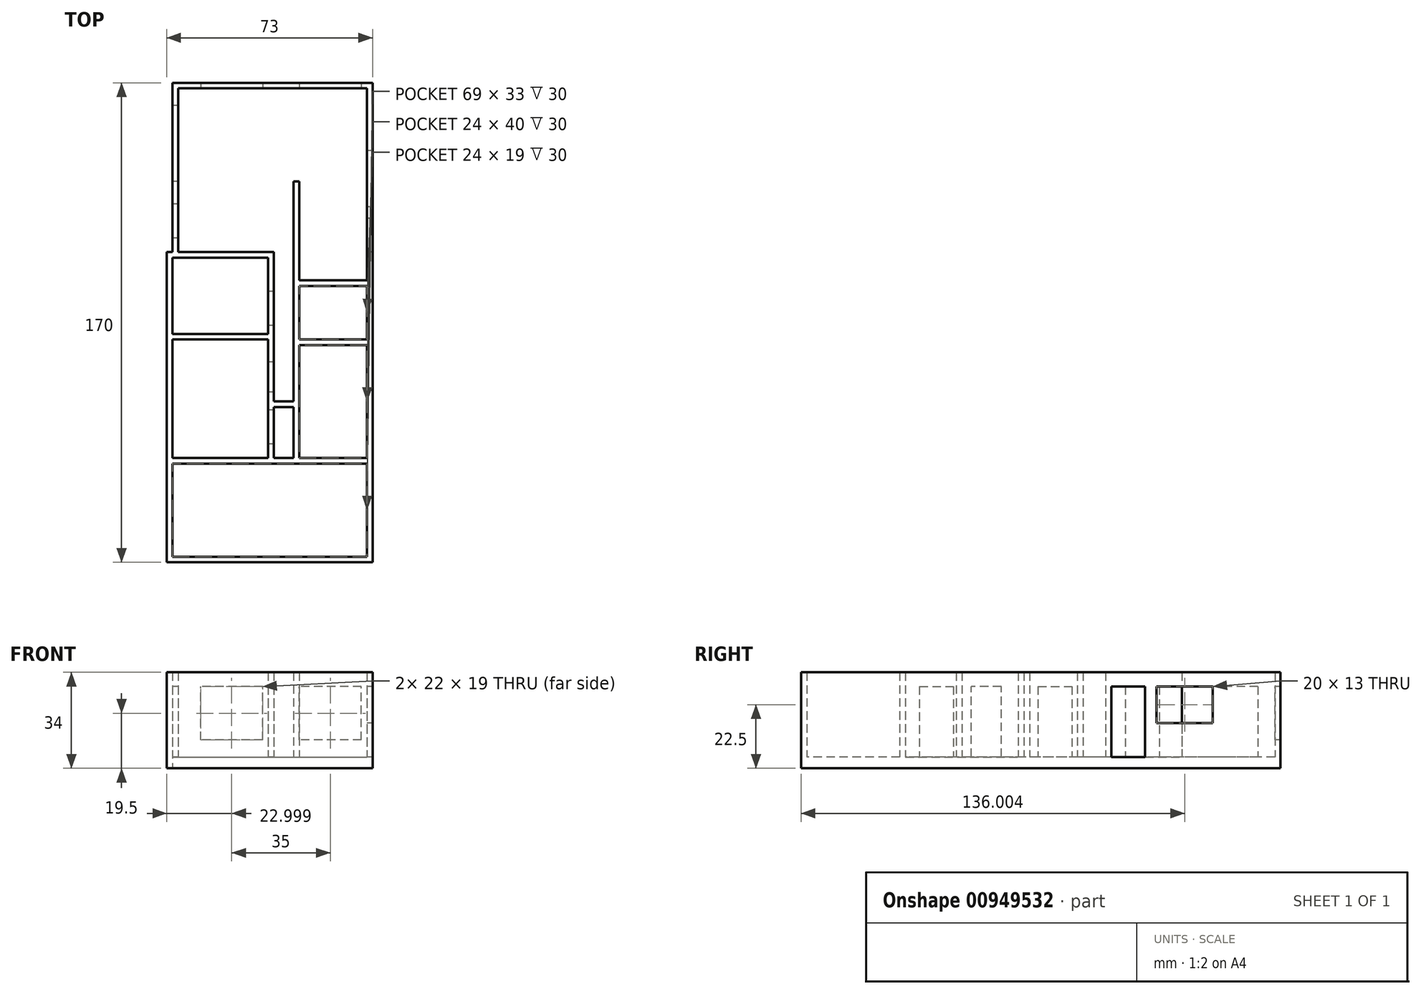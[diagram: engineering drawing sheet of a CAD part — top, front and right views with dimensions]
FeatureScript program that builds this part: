
annotation { "Feature Type Name" : "Feature", "Feature Type Description" : "" }
export const myFeature = defineFeature(function(context is Context, id is Id, definition is map)
    precondition{}
    {
        {
            assignVariable(context, id + "F0", {"name" : "WallWidth", "anyValue" : 2});
        }
        {
            assignVariable(context, id + "F1", {"name" : "Floor", "anyValue" : 4});
        }
        {
            var Q0;
            Q0=qCreatedBy(makeId("Top.planeOp"),FACE);
            var sketch = newSketch(context, id + "F2", { "sketchPlane" : qUnion([Q0])});
            skLineSegment(sketch, "E0.bottom", {"start": v(-13.18, 167.27) * mm, "end": v(57.82, 167.27) * mm});
            skLineSegment(sketch, "E0.top", {"start": v(-13.18, -2.73) * mm, "end": v(57.82, -2.73) * mm});
            skLineSegment(sketch, "E0.left", {"start": v(-13.18, 167.27) * mm, "end": v(-13.18, -2.73) * mm});
            skLineSegment(sketch, "E0.right", {"start": v(57.82, 167.27) * mm, "end": v(57.82, -2.73) * mm});
            skLineSegment(sketch, "E1.bottom", {"start": v(-13.18, -2.73) * mm, "end": v(-15.18, -2.73) * mm});
            skLineSegment(sketch, "E1.top", {"start": v(-13.18, 107.27) * mm, "end": v(-15.18, 107.27) * mm});
            skLineSegment(sketch, "E1.left", {"start": v(-13.18, -2.73) * mm, "end": v(-13.18, 107.27) * mm});
            skLineSegment(sketch, "E1.right", {"start": v(-15.18, -2.73) * mm, "end": v(-15.18, 107.27) * mm});
            skSolve(sketch);
        }
        {
            var Q0;
            Q0=qSketchRegion(id+"F2",true);
            extrude(context, id + "F3", {"entities" : qUnion([Q0]), "depth" : (getVariable(context, 'Floor')) * mm, "offsetDistance" : 25 * mm});
        }
        {
            var Q0;
            Q0=makeQuery(id+"F3.opExtrude","CAP_FACE",FACE,{"disambiguationData":[OSD([sQuery(id+"F2.wireOp",EDGE,"E0.bottom"),sQuery(id+"F2.wireOp",EDGE,"E0.top"),sQuery(id+"F2.wireOp",EDGE,"E0.left"),sQuery(id+"F2.wireOp",EDGE,"E0.right"),sQuery(id+"F2.wireOp",EDGE,"E1.bottom"),sQuery(id+"F2.wireOp",EDGE,"E1.top"),sQuery(id+"F2.wireOp",EDGE,"E1.right")])],"isStart":false});
            var sketch = newSketch(context, id + "F4", { "sketchPlane" : qUnion([Q0])});
            skLineSegment(sketch, "E2.bottom", {"start": v(-15.18, -2.73) * mm, "end": v(57.82, -2.73) * mm});
            skLineSegment(sketch, "E2.top", {"start": v(-15.18, -0.73) * mm, "end": v(57.82, -0.73) * mm});
            skLineSegment(sketch, "E2.left", {"start": v(-15.18, -2.73) * mm, "end": v(-15.18, -0.73) * mm});
            skLineSegment(sketch, "E2.right", {"start": v(57.82, -2.73) * mm, "end": v(57.82, -0.73) * mm});
            skLineSegment(sketch, "E3.bottom", {"start": v(25.82, 32.27) * mm, "end": v(27.82, 32.27) * mm});
            skLineSegment(sketch, "E3.top", {"start": v(25.82, -0.73) * mm, "end": v(27.82, -0.73) * mm});
            skLineSegment(sketch, "E3.left", {"start": v(25.82, 32.27) * mm, "end": v(25.82, -0.73) * mm});
            skLineSegment(sketch, "E3.right", {"start": v(27.82, 32.27) * mm, "end": v(27.82, -0.73) * mm});
            skLineSegment(sketch, "E4.bottom", {"start": v(-15.18, 107.27) * mm, "end": v(-13.18, 107.27) * mm});
            skLineSegment(sketch, "E4.top", {"start": v(-15.18, -0.73) * mm, "end": v(-13.18, -0.73) * mm});
            skLineSegment(sketch, "E4.left", {"start": v(-15.18, 107.27) * mm, "end": v(-15.18, -0.73) * mm});
            skLineSegment(sketch, "E4.right", {"start": v(-13.18, 107.27) * mm, "end": v(-13.18, -0.73) * mm});
            skLineSegment(sketch, "E5.bottom", {"start": v(55.82, 32.27) * mm, "end": v(57.82, 32.27) * mm});
            skLineSegment(sketch, "E5.top", {"start": v(55.82, -0.73) * mm, "end": v(57.82, -0.73) * mm});
            skLineSegment(sketch, "E5.left", {"start": v(55.82, 32.27) * mm, "end": v(55.82, -0.73) * mm});
            skLineSegment(sketch, "E5.right", {"start": v(57.82, 32.27) * mm, "end": v(57.82, -0.73) * mm});
            skLineSegment(sketch, "E6.bottom", {"start": v(-13.18, 34.27) * mm, "end": v(57.82, 34.27) * mm});
            skLineSegment(sketch, "E6.top", {"start": v(-13.18, 32.27) * mm, "end": v(57.82, 32.27) * mm});
            skLineSegment(sketch, "E6.left", {"start": v(-13.18, 34.27) * mm, "end": v(-13.18, 32.27) * mm});
            skLineSegment(sketch, "E6.right", {"start": v(57.82, 34.27) * mm, "end": v(57.82, 32.27) * mm});
            skLineSegment(sketch, "E7.bottom", {"start": v(55.82, 34.27) * mm, "end": v(57.82, 34.27) * mm});
            skLineSegment(sketch, "E7.top", {"start": v(55.82, 74.27) * mm, "end": v(57.82, 74.27) * mm});
            skLineSegment(sketch, "E7.left", {"start": v(55.82, 34.27) * mm, "end": v(55.82, 74.27) * mm});
            skLineSegment(sketch, "E7.right", {"start": v(57.82, 34.27) * mm, "end": v(57.82, 74.27) * mm});
            skLineSegment(sketch, "E8.bottom", {"start": v(29.82, 76.27) * mm, "end": v(57.82, 76.27) * mm});
            skLineSegment(sketch, "E8.top", {"start": v(29.82, 74.27) * mm, "end": v(57.82, 74.27) * mm});
            skLineSegment(sketch, "E8.left", {"start": v(29.82, 76.27) * mm, "end": v(29.82, 74.27) * mm});
            skLineSegment(sketch, "E8.right", {"start": v(57.82, 76.27) * mm, "end": v(57.82, 74.27) * mm});
            skLineSegment(sketch, "E9.bottom", {"start": v(-13.18, 78.27) * mm, "end": v(22.82, 78.27) * mm});
            skLineSegment(sketch, "E9.top", {"start": v(-13.18, 76.27) * mm, "end": v(22.82, 76.27) * mm});
            skLineSegment(sketch, "E9.left", {"start": v(-13.18, 78.27) * mm, "end": v(-13.18, 76.27) * mm});
            skLineSegment(sketch, "E9.right", {"start": v(22.82, 78.27) * mm, "end": v(22.82, 76.27) * mm});
            skLineSegment(sketch, "E10.bottom", {"start": v(22.82, 76.27) * mm, "end": v(20.82, 76.27) * mm});
            skLineSegment(sketch, "E10.top", {"start": v(22.82, 34.27) * mm, "end": v(20.82, 34.27) * mm});
            skLineSegment(sketch, "E10.left", {"start": v(22.82, 76.27) * mm, "end": v(22.82, 34.27) * mm});
            skLineSegment(sketch, "E10.right", {"start": v(20.82, 76.27) * mm, "end": v(20.82, 34.27) * mm});
            skLineSegment(sketch, "E11.bottom", {"start": v(29.82, 74.27) * mm, "end": v(31.82, 74.27) * mm});
            skLineSegment(sketch, "E11.top", {"start": v(29.82, 34.27) * mm, "end": v(31.82, 34.27) * mm});
            skLineSegment(sketch, "E11.left", {"start": v(29.82, 74.27) * mm, "end": v(29.82, 34.27) * mm});
            skLineSegment(sketch, "E11.right", {"start": v(31.82, 74.27) * mm, "end": v(31.82, 34.27) * mm});
            skLineSegment(sketch, "E12.bottom", {"start": v(-13.18, 107.27) * mm, "end": v(22.82, 107.27) * mm});
            skLineSegment(sketch, "E12.top", {"start": v(-13.18, 105.27) * mm, "end": v(22.82, 105.27) * mm});
            skLineSegment(sketch, "E12.left", {"start": v(-13.18, 107.27) * mm, "end": v(-13.18, 105.27) * mm});
            skLineSegment(sketch, "E12.right", {"start": v(22.82, 107.27) * mm, "end": v(22.82, 105.27) * mm});
            skLineSegment(sketch, "E13.bottom", {"start": v(22.82, 105.27) * mm, "end": v(20.82, 105.27) * mm});
            skLineSegment(sketch, "E13.top", {"start": v(22.82, 78.27) * mm, "end": v(20.82, 78.27) * mm});
            skLineSegment(sketch, "E13.left", {"start": v(22.82, 105.27) * mm, "end": v(22.82, 78.27) * mm});
            skLineSegment(sketch, "E13.right", {"start": v(20.82, 105.27) * mm, "end": v(20.82, 78.27) * mm});
            skLineSegment(sketch, "E14.bottom", {"start": v(-13.18, 167.27) * mm, "end": v(-11.18, 167.27) * mm});
            skLineSegment(sketch, "E14.top", {"start": v(-13.18, 107.27) * mm, "end": v(-11.18, 107.27) * mm});
            skLineSegment(sketch, "E14.left", {"start": v(-13.18, 167.27) * mm, "end": v(-13.18, 107.27) * mm});
            skLineSegment(sketch, "E14.right", {"start": v(-11.18, 167.27) * mm, "end": v(-11.18, 107.27) * mm});
            skLineSegment(sketch, "E15.bottom", {"start": v(-11.18, 167.27) * mm, "end": v(57.82, 167.27) * mm});
            skLineSegment(sketch, "E15.top", {"start": v(-11.18, 165.27) * mm, "end": v(57.82, 165.27) * mm});
            skLineSegment(sketch, "E15.left", {"start": v(-11.18, 167.27) * mm, "end": v(-11.18, 165.27) * mm});
            skLineSegment(sketch, "E15.right", {"start": v(57.82, 167.27) * mm, "end": v(57.82, 165.27) * mm});
            skLineSegment(sketch, "E16.bottom", {"start": v(57.82, 165.27) * mm, "end": v(55.82, 165.27) * mm});
            skLineSegment(sketch, "E16.top", {"start": v(57.82, 76.27) * mm, "end": v(55.82, 76.27) * mm});
            skLineSegment(sketch, "E16.left", {"start": v(57.82, 165.27) * mm, "end": v(57.82, 76.27) * mm});
            skLineSegment(sketch, "E16.right", {"start": v(55.82, 165.27) * mm, "end": v(55.82, 76.27) * mm});
            skLineSegment(sketch, "E17.bottom", {"start": v(29.82, 97.27) * mm, "end": v(55.82, 97.27) * mm});
            skLineSegment(sketch, "E17.top", {"start": v(29.82, 95.27) * mm, "end": v(55.82, 95.27) * mm});
            skLineSegment(sketch, "E17.left", {"start": v(29.82, 97.27) * mm, "end": v(29.82, 95.27) * mm});
            skLineSegment(sketch, "E17.right", {"start": v(55.82, 97.27) * mm, "end": v(55.82, 95.27) * mm});
            skLineSegment(sketch, "E18.bottom", {"start": v(29.82, 97.27) * mm, "end": v(31.82, 97.27) * mm});
            skLineSegment(sketch, "E18.top", {"start": v(29.82, 132.27) * mm, "end": v(31.82, 132.27) * mm});
            skLineSegment(sketch, "E18.left", {"start": v(29.82, 97.27) * mm, "end": v(29.82, 132.27) * mm});
            skLineSegment(sketch, "E18.right", {"start": v(31.82, 97.27) * mm, "end": v(31.82, 132.27) * mm});
            skLineSegment(sketch, "E19.bottom", {"start": v(29.82, 95.27) * mm, "end": v(31.82, 95.27) * mm});
            skLineSegment(sketch, "E19.top", {"start": v(29.82, 76.27) * mm, "end": v(31.82, 76.27) * mm});
            skLineSegment(sketch, "E19.left", {"start": v(29.82, 95.27) * mm, "end": v(29.82, 76.27) * mm});
            skLineSegment(sketch, "E19.right", {"start": v(31.82, 95.27) * mm, "end": v(31.82, 76.27) * mm});
            skLineSegment(sketch, "E20.bottom", {"start": v(22.82, 52.27) * mm, "end": v(29.82, 52.27) * mm});
            skLineSegment(sketch, "E20.top", {"start": v(22.82, 54.27) * mm, "end": v(29.82, 54.27) * mm});
            skLineSegment(sketch, "E20.left", {"start": v(22.82, 52.27) * mm, "end": v(22.82, 54.27) * mm});
            skLineSegment(sketch, "E20.right", {"start": v(29.82, 52.27) * mm, "end": v(29.82, 54.27) * mm});
            skSolve(sketch);
        }
        {
            var Q0;
            {var subQ2=sQuery(id+"F4.wireOp",EDGE,"E3.bottom");var subQ19=sQuery(id+"F4.wireOp",EDGE,"E5.bottom");var subQ20=makeQuery(id+"F4.imprint","IMPRINT",EDGE,{"derivedFrom":subQ19});var subQ23=sQuery(id+"F4.wireOp",EDGE,"E16.left");var subQ31=sQuery(id+"F4.wireOp",EDGE,"E7.top");var subQ32=makeQuery(id+"F4.imprint","IMPRINT",EDGE,{"derivedFrom":subQ31});var subQ37=sQuery(id+"F4.wireOp",EDGE,"E4.bottom");var subQ59=sQuery(id+"F4.wireOp",EDGE,"E12.right");var subQ67=sQuery(id+"F4.wireOp",EDGE,"E15.bottom");var subQ68=sQuery(id+"F4.wireOp",EDGE,"E14.bottom");Q0=qUnion([makeQuery(id+"F4.imprint","IMPRINT",FACE,{"disambiguationData":[TD([[subQ20,-1.0]])]}),makeQuery(id+"F4.imprint","IMPRINT",FACE,{"disambiguationData":[TD([[subQ32,-1.0]])]}),makeQuery(id+"F4.imprint","IMPRINT",FACE,{"disambiguationData":[TD([[makeQuery(id+"F4.imprint","IMPRINT",EDGE,{"derivedFrom":subQ68}),-1.0]])]}),makeQuery(id+"F4.imprint","IMPRINT",FACE,{"disambiguationData":[TD([[makeQuery(id+"F4.imprint","IMPRINT",EDGE,{"derivedFrom":subQ67}),-1.0]])]}),makeQuery(id+"F4.imprint","IMPRINT",FACE,{"disambiguationData":[TD([[makeQuery(id+"F4.imprint","IMPRINT",EDGE,{"derivedFrom":sQuery(id+"F4.wireOp",EDGE,"E2.bottom")}),1.0]])]}),makeQuery(id+"F4.imprint","IMPRINT",FACE,{"disambiguationData":[TD([[makeQuery(id+"F4.imprint","IMPRINT",EDGE,{"derivedFrom":subQ59}),-1.0]])]}),makeQuery(id+"F4.imprint","IMPRINT",FACE,{"disambiguationData":[TD([[makeQuery(id+"F4.imprint","IMPRINT",EDGE,{"derivedFrom":subQ23}),-1.0]])]}),makeQuery(id+"F4.imprint","IMPRINT",FACE,{"disambiguationData":[TD([[makeQuery(id+"F4.imprint","IMPRINT",EDGE,{"derivedFrom":subQ37}),1.0]])]}),makeQuery(id+"F4.imprint","IMPRINT",FACE,{"disambiguationData":[TD([[subQ32,1.0]])]}),makeQuery(id+"F4.imprint","IMPRINT",FACE,{"disambiguationData":[TD([[makeQuery(id+"F4.imprint","IMPRINT",EDGE,{"derivedFrom":subQ2}),1.0]])]})]);}
            var Q1;
            {var subQ0=sQuery(id+"F4.wireOp",EDGE,"E13.left");Q1=makeQuery(id+"F4.imprint","IMPRINT",FACE,{"disambiguationData":[TD([[makeQuery(id+"F4.imprint","IMPRINT",EDGE,{"derivedFrom":subQ0}),-1.0]])]});}
            var Q2;
            {var subQ4=sQuery(id+"F4.wireOp",EDGE,"E10.right");Q2=makeQuery(id+"F4.imprint","IMPRINT",FACE,{"disambiguationData":[TD([[makeQuery(id+"F4.imprint","IMPRINT",EDGE,{"derivedFrom":subQ4}),1.0]])]});}
            var Q3;
            {var subQ7=sQuery(id+"F4.wireOp",EDGE,"E9.right");Q3=makeQuery(id+"F4.imprint","IMPRINT",FACE,{"disambiguationData":[TD([[makeQuery(id+"F4.imprint","IMPRINT",EDGE,{"derivedFrom":subQ7}),-1.0]])]});}
            var Q4;
            {var subQ2=sQuery(id+"F4.wireOp",EDGE,"E19.left");Q4=makeQuery(id+"F4.imprint","IMPRINT",FACE,{"disambiguationData":[TD([[makeQuery(id+"F4.imprint","IMPRINT",EDGE,{"derivedFrom":subQ2}),1.0]])]});}
            var Q5;
            {var subQ6=sQuery(id+"F4.wireOp",EDGE,"E17.left");Q5=makeQuery(id+"F4.imprint","IMPRINT",FACE,{"disambiguationData":[TD([[makeQuery(id+"F4.imprint","IMPRINT",EDGE,{"derivedFrom":subQ6}),1.0]])]});}
            var Q6;
            Q6=makeQuery(id+"F4.imprint","IMPRINT",FACE,{"disambiguationData":[TD([[makeQuery(id+"F4.imprint","IMPRINT",EDGE,{"derivedFrom":sQuery(id+"F4.wireOp",EDGE,"E18.top")}),-1.0]])]});
            var Q7;
            {var subQ4=sQuery(id+"F4.wireOp",EDGE,"E11.right");Q7=makeQuery(id+"F4.imprint","IMPRINT",FACE,{"disambiguationData":[TD([[makeQuery(id+"F4.imprint","IMPRINT",EDGE,{"derivedFrom":subQ4}),-1.0]])]});}
            var Q8;
            {var subQ0=sQuery(id+"F4.wireOp",EDGE,"E20.bottom");Q8=makeQuery(id+"F4.imprint","IMPRINT",FACE,{"disambiguationData":[TD([[makeQuery(id+"F4.imprint","IMPRINT",EDGE,{"derivedFrom":subQ0}),1.0]])]});}
            extrude(context, id + "F5", {"entities" : qUnion([Q0, Q1, Q2, Q3, Q4, Q5, Q6, Q7, Q8]), "operationType" : NewBodyOperationType.ADD, "depth" : 30 * mm, "offsetDistance" : 25 * mm});
        }
        {
            var Q0;
            Q0=makeQuery(id+"F5.boolean.opBoolean","MERGE",FACE,{"derivedFrom":[makeQuery(id+"F3.opExtrude","SWEPT_FACE",FACE,{"disambiguationData":[OSD([sQuery(id+"F2.wireOp",EDGE,"E0.left")])]}),makeQuery(id+"F5.opExtrude","SWEPT_FACE",FACE,{"disambiguationData":[OSD([sQuery(id+"F4.wireOp",EDGE,"E14.left")])]})]});
            var sketch = newSketch(context, id + "F6", { "sketchPlane" : qUnion([Q0])});
            skLineSegment(sketch, "E21.bottom", {"start": v(-124.27, 29) * mm, "end": v(-112.27, 29) * mm});
            skLineSegment(sketch, "E21.top", {"start": v(-124.27, 4) * mm, "end": v(-112.27, 4) * mm});
            skLineSegment(sketch, "E21.left", {"start": v(-124.27, 29) * mm, "end": v(-124.27, 4) * mm});
            skLineSegment(sketch, "E21.right", {"start": v(-112.27, 29) * mm, "end": v(-112.27, 4) * mm});
            skLineSegment(sketch, "E22.bottom", {"start": v(-159.27, 29) * mm, "end": v(-132.27, 29) * mm});
            skLineSegment(sketch, "E22.top", {"start": v(-159.27, 4) * mm, "end": v(-132.27, 4) * mm});
            skLineSegment(sketch, "E22.left", {"start": v(-159.27, 29) * mm, "end": v(-159.27, 4) * mm});
            skLineSegment(sketch, "E22.right", {"start": v(-132.27, 29) * mm, "end": v(-132.27, 4) * mm});
            skSolve(sketch);
        }
        {
            var Q0;
            Q0=qSketchRegion(id+"F6",true);
            extrude(context, id + "F7", {"entities" : qUnion([Q0]), "operationType" : NewBodyOperationType.REMOVE, "oppositeDirection" : true, "depth" : (getVariable(context, 'WallWidth')) * mm, "offsetDistance" : 25 * mm});
        }
        {
            var Q0;
            {var subQ0=sQuery(id+"F4.wireOp",EDGE,"E16.right");Q0=makeQuery(id+"F5.opExtrude","SWEPT_FACE",FACE,{"disambiguationData":[OSD([subQ0]),TDD([makeQuery(id+"F4.imprint","IMPRINT",EDGE,{"disambiguationData":[TD([[makeQuery(id+"F4.imprint","INTERSECT",VERTEX,{"derivedFrom":[sQuery(id+"F4.wireOp",EDGE,"E15.top"),subQ0]}),-1.0]])],"derivedFrom":subQ0})])]});}
            var sketch = newSketch(context, id + "F8", { "sketchPlane" : qUnion([Q0])});
            skLineSegment(sketch, "E23.bottom", {"start": v(-107.27, 29) * mm, "end": v(-119.27, 29) * mm});
            skLineSegment(sketch, "E23.top", {"start": v(-107.27, 4) * mm, "end": v(-119.27, 4) * mm});
            skLineSegment(sketch, "E23.left", {"start": v(-107.27, 29) * mm, "end": v(-107.27, 4) * mm});
            skLineSegment(sketch, "E23.right", {"start": v(-119.27, 29) * mm, "end": v(-119.27, 4) * mm});
            skLineSegment(sketch, "E24.bottom", {"start": v(-123.27, 29) * mm, "end": v(-143.27, 29) * mm});
            skLineSegment(sketch, "E24.top", {"start": v(-123.27, 16) * mm, "end": v(-143.27, 16) * mm});
            skLineSegment(sketch, "E24.left", {"start": v(-123.27, 29) * mm, "end": v(-123.27, 16) * mm});
            skLineSegment(sketch, "E24.right", {"start": v(-143.27, 29) * mm, "end": v(-143.27, 16) * mm});
            skSolve(sketch);
        }
        {
            var Q0;
            Q0=qSketchRegion(id+"F8",true);
            extrude(context, id + "F9", {"entities" : qUnion([Q0]), "operationType" : NewBodyOperationType.REMOVE, "oppositeDirection" : true, "depth" : (getVariable(context, 'WallWidth')) * mm, "offsetDistance" : 25 * mm});
        }
        {
            var Q0;
            Q0=makeQuery(id+"F5.opExtrude","SWEPT_FACE",FACE,{"disambiguationData":[OSD([sQuery(id+"F4.wireOp",EDGE,"E15.top")])]});
            var sketch = newSketch(context, id + "F10", { "sketchPlane" : qUnion([Q0])});
            skLineSegment(sketch, "E25.bottom", {"start": v(53.82, 10) * mm, "end": v(31.82, 10) * mm});
            skLineSegment(sketch, "E25.top", {"start": v(53.82, 29) * mm, "end": v(31.82, 29) * mm});
            skLineSegment(sketch, "E25.left", {"start": v(53.82, 10) * mm, "end": v(53.82, 29) * mm});
            skLineSegment(sketch, "E25.right", {"start": v(31.82, 10) * mm, "end": v(31.82, 29) * mm});
            skLineSegment(sketch, "E26.bottom", {"start": v(18.82, 10) * mm, "end": v(-3.18, 10) * mm});
            skLineSegment(sketch, "E26.top", {"start": v(18.82, 29) * mm, "end": v(-3.18, 29) * mm});
            skLineSegment(sketch, "E26.left", {"start": v(18.82, 10) * mm, "end": v(18.82, 29) * mm});
            skLineSegment(sketch, "E26.right", {"start": v(-3.18, 10) * mm, "end": v(-3.18, 29) * mm});
            skSolve(sketch);
        }
        {
            var Q0;
            Q0=qSketchRegion(id+"F10",true);
            extrude(context, id + "F11", {"entities" : qUnion([Q0]), "operationType" : NewBodyOperationType.REMOVE, "oppositeDirection" : true, "depth" : (getVariable(context, 'WallWidth')) * mm, "offsetDistance" : 25 * mm});
        }
        {
            var Q0;
            Q0=makeQuery(id+"F5.opExtrude","SWEPT_FACE",FACE,{"disambiguationData":[OSD([sQuery(id+"F4.wireOp",EDGE,"E13.right")])]});
            var sketch = newSketch(context, id + "F12", { "sketchPlane" : qUnion([Q0])});
            skLineSegment(sketch, "E27.bottom", {"start": v(-81.27, 29) * mm, "end": v(-93.27, 29) * mm});
            skLineSegment(sketch, "E27.top", {"start": v(-81.27, 4) * mm, "end": v(-93.27, 4) * mm});
            skLineSegment(sketch, "E27.left", {"start": v(-81.27, 29) * mm, "end": v(-81.27, 4) * mm});
            skLineSegment(sketch, "E27.right", {"start": v(-93.27, 29) * mm, "end": v(-93.27, 4) * mm});
            skLineSegment(sketch, "E28.bottom", {"start": v(-68.27, 4) * mm, "end": v(-57.64, 4) * mm});
            skLineSegment(sketch, "E28.top", {"start": v(-68.27, 29) * mm, "end": v(-57.64, 29) * mm});
            skLineSegment(sketch, "E28.left", {"start": v(-68.27, 4) * mm, "end": v(-68.27, 29) * mm});
            skLineSegment(sketch, "E28.right", {"start": v(-57.64, 4) * mm, "end": v(-57.64, 29) * mm});
            skLineSegment(sketch, "E29.bottom", {"start": v(-39.27, 29) * mm, "end": v(-51.27, 29) * mm});
            skLineSegment(sketch, "E29.top", {"start": v(-39.27, 4) * mm, "end": v(-51.27, 4) * mm});
            skLineSegment(sketch, "E29.left", {"start": v(-39.27, 29) * mm, "end": v(-39.27, 4) * mm});
            skLineSegment(sketch, "E29.right", {"start": v(-51.27, 29) * mm, "end": v(-51.27, 4) * mm});
            skSolve(sketch);
        }
        {
            var Q0;
            Q0=qSketchRegion(id+"F12",true);
            extrude(context, id + "F13", {"entities" : qUnion([Q0]), "operationType" : NewBodyOperationType.REMOVE, "oppositeDirection" : true, "depth" : (getVariable(context, 'WallWidth')) * mm, "offsetDistance" : 25 * mm});
        }
    });
